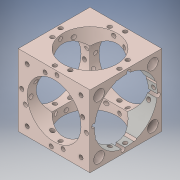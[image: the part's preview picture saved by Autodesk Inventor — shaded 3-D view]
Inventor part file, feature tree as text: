
AUTODESK INVENTOR PART (.ipt)
format: ipt  version: 2016 (Build 200138000, 138)  size: 645,120 bytes
history: native  units: mm
features: thread x56, other x2, extrude x1, sketch x1, projected_geometry x1
ambient origin geometry x8: Origin, YZ Plane, XZ Plane, XY Plane, X Axis, Y Axis, Z Axis, Center Point
bodies: Solid1 (feature_tree)
feature tree (61):
  other  "Cube_30.iam"
  other  "00012269.ipt:1"
  thread  "GEWINDEHUELSE.ipt:1"  [1 undecoded]
  thread  "GEWINDEHUELSE_1.ipt:1"  [1 undecoded]
  thread  "GEWINDEHUELSE_2.ipt:1"  [1 undecoded]
  thread  "GEWINDEHUELSE_3.ipt:1"  [1 undecoded]
  thread  "GEWINDEHUELSE_4.ipt:1"  [1 undecoded]
  thread  "GEWINDEHUELSE_5.ipt:1"  [1 undecoded]
  thread  "GEWINDEHUELSE_6.ipt:1"  [1 undecoded]
  thread  "GEWINDEHUELSE_7.ipt:1"  [1 undecoded]
  thread  "GEWINDEHUELSE_8.ipt:1"  [1 undecoded]
  thread  "GEWINDEHUELSE_9.ipt:1"  [1 undecoded]
  thread  "GEWINDEHUELSE_10.ipt:1"  [1 undecoded]
  thread  "GEWINDEHUELSE_11.ipt:1"  [1 undecoded]
  thread  "GEWINDEHUELSE_12.ipt:1"  [1 undecoded]
  thread  "GEWINDEHUELSE_13.ipt:1"  [1 undecoded]
  thread  "GEWINDEHUELSE_14.ipt:1"  [1 undecoded]
  thread  "GEWINDEHUELSE_15.ipt:1"  [1 undecoded]
  thread  "GEWINDEHUELSE_16.ipt:1"  [1 undecoded]
  thread  "GEWINDEHUELSE_17.ipt:1"  [1 undecoded]
  thread  "GEWINDEHUELSE_18.ipt:1"  [1 undecoded]
  thread  "GEWINDEHUELSE_19.ipt:1"  [1 undecoded]
  thread  "GEWINDEHUELSE_20.ipt:1"  [1 undecoded]
  thread  "GEWINDEHUELSE_21.ipt:1"  [1 undecoded]
  thread  "GEWINDEHUELSE_22.ipt:1"  [1 undecoded]
  thread  "GEWINDEHUELSE_23.ipt:1"  [1 undecoded]
  thread  "GEWINDEHUELSE_24.ipt:1"  [1 undecoded]
  thread  "GEWINDEHUELSE_25.ipt:1"  [1 undecoded]
  thread  "GEWINDEHUELSE_26.ipt:1"  [1 undecoded]
  thread  "GEWINDEHUELSE_27.ipt:1"  [1 undecoded]
  thread  "GEWINDEHUELSE_28.ipt:1"  [1 undecoded]
  thread  "GEWINDEHUELSE_29.ipt:1"  [1 undecoded]
  thread  "GEWINDEHUELSE_30.ipt:1"  [1 undecoded]
  thread  "GEWINDEHUELSE_31.ipt:1"  [1 undecoded]
  thread  "GEWINDEHUELSE_32.ipt:1"  [1 undecoded]
  thread  "GEWINDEHUELSE_33.ipt:1"  [1 undecoded]
  thread  "GEWINDEHUELSE_34.ipt:1"  [1 undecoded]
  thread  "GEWINDEHUELSE_35.ipt:1"  [1 undecoded]
  thread  "GEWINDEHUELSE_36.ipt:1"  [1 undecoded]
  thread  "GEWINDEHUELSE_37.ipt:1"  [1 undecoded]
  thread  "GEWINDEHUELSE_38.ipt:1"  [1 undecoded]
  thread  "GEWINDEHUELSE_39.ipt:1"  [1 undecoded]
  thread  "GEWINDEHUELSE_40.ipt:1"  [1 undecoded]
  thread  "GEWINDEHUELSE_41.ipt:1"  [1 undecoded]
  thread  "GEWINDEHUELSE_42.ipt:1"  [1 undecoded]
  thread  "GEWINDEHUELSE_43.ipt:1"  [1 undecoded]
  thread  "GEWINDEHUELSE_44.ipt:1"  [1 undecoded]
  thread  "GEWINDEHUELSE_45.ipt:1"  [1 undecoded]
  thread  "GEWINDEHUELSE_46.ipt:1"  [1 undecoded]
  thread  "GEWINDEHUELSE_47.ipt:1"  [1 undecoded]
  thread  "GEWINDEHUELSE_48.ipt:1"  [1 undecoded]
  thread  "GEWINDEHUELSE_49.ipt:1"  [1 undecoded]
  thread  "GEWINDEHUELSE_50.ipt:1"  [1 undecoded]
  thread  "GEWINDEHUELSE_51.ipt:1"  [1 undecoded]
  thread  "GEWINDEHUELSE_52.ipt:1"  [1 undecoded]
  thread  "GEWINDEHUELSE_53.ipt:1"  [1 undecoded]
  thread  "GEWINDEHUELSE_54.ipt:1"  [1 undecoded]
  thread  "GEWINDEHUELSE_55.ipt:1"  [1 undecoded]
  extrude  "Extrusion1"  [1 undecoded]
  sketch  "Sketch1"
  projected_geometry  "Projected Loop1"
note: 57 required parameter values undecoded (feature->parameter linkage not recoverable at this tier; creation-order binding heuristic only, values carry confidence <= 0.55)
